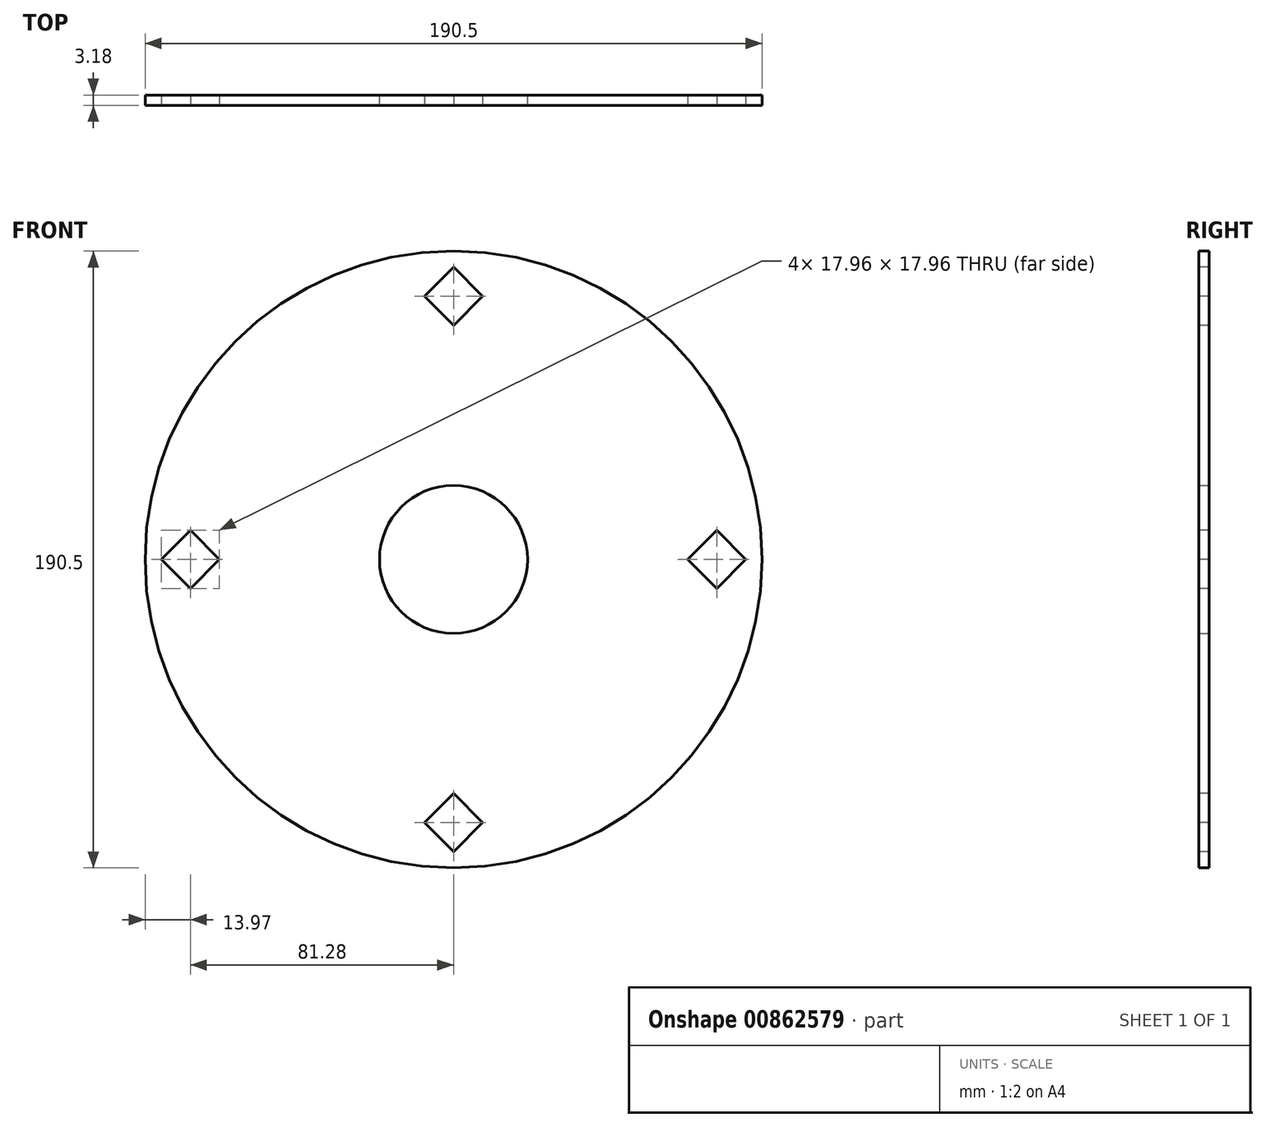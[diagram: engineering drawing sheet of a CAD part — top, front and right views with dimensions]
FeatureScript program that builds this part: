
annotation { "Feature Type Name" : "Feature", "Feature Type Description" : "" }
export const myFeature = defineFeature(function(context is Context, id is Id, definition is map)
    precondition{}
    {
        {
            var Q0;
            Q0=qCreatedBy(makeId("Front.planeOp"),FACE);
            var sketch = newSketch(context, id + "F0", { "sketchPlane" : qUnion([Q0])});
            skCircle(sketch, "E0", {"center": v(0, 0) * mm, "radius": 95.25 * mm});
            skSolve(sketch);
        }
        {
            var Q0;
            Q0=makeQuery(id+"F0.imprint","IMPRINT",FACE,{"disambiguationData":[TD([[makeQuery(id+"F0.imprint","IMPRINT",EDGE,{"derivedFrom":sQuery(id+"F0.wireOp",EDGE,"E0")}),1.0]])]});
            var sketch = newSketch(context, id + "F1", { "sketchPlane" : qUnion([Q0])});
            skCircle(sketch, "E1", {"center": v(0, 0) * mm, "radius": 22.86 * mm});
            skSolve(sketch);
        }
        {
            var Q0;
            Q0 = qSketchRegion(id + "F0", true);
            extrude(context, id + "F2", {"entities" : qUnion([Q0]), "depth" : 3.17 * mm, "offsetDistance" : 25.4 * mm});
        }
        {
            var Q0;
            Q0 = qSketchRegion(id + "F1", true);
            extrude(context, id + "F3", {"entities" : qUnion([Q0]), "operationType" : NewBodyOperationType.REMOVE, "depth" : 25.4 * mm, "offsetDistance" : 25.4 * mm});
        }
        {
            var Q0;
            Q0=makeQuery(id+"F2.opExtrude","CAP_FACE",FACE,{"disambiguationData":[OSD([sQuery(id+"F0.wireOp",EDGE,"E0")])],"isStart":false});
            var sketch = newSketch(context, id + "F4", { "sketchPlane" : qUnion([Q0])});
            skLineSegment(sketch, "E2", {"start": v(0, 0) * mm, "end": v(0, 95.25) * mm, "construction": true});
            skLineSegment(sketch, "E3.bottom", {"start": v(-72.3, 0) * mm, "end": v(-81.28, 8.98) * mm});
            skLineSegment(sketch, "E3.top", {"start": v(-81.28, -8.98) * mm, "end": v(-90.26, 0) * mm});
            skLineSegment(sketch, "E3.left", {"start": v(-72.3, 0) * mm, "end": v(-81.28, -8.98) * mm});
            skLineSegment(sketch, "E3.right", {"start": v(-81.28, 8.98) * mm, "end": v(-90.26, 0) * mm});
            skPoint(sketch, "E3.middle", {"position": v(-81.28, 0) * mm});
            skPoint(sketch, "E4.center", {"position": v(0, 0) * mm});
            skLineSegment(sketch, "E5", {"start": v(0, 0) * mm, "end": v(-81.28, 0) * mm, "construction": true});
            skPoint(sketch, "E6.center", {"position": v(-17.11, 0) * mm});
            skLineSegment(sketch, "E7.1.0", {"start": v(8.98, -81.28) * mm, "end": v(0, -90.26) * mm});
            skPoint(sketch, "E7.1.1", {"position": v(0, -81.28) * mm});
            skLineSegment(sketch, "E7.1.2", {"start": v(0, -72.3) * mm, "end": v(-8.98, -81.28) * mm});
            skLineSegment(sketch, "E7.1.3", {"start": v(-8.98, -81.28) * mm, "end": v(0, -90.26) * mm});
            skLineSegment(sketch, "E7.1.4", {"start": v(0, -72.3) * mm, "end": v(8.98, -81.28) * mm});
            skLineSegment(sketch, "E7.2.0", {"start": v(81.28, 8.98) * mm, "end": v(90.26, 0) * mm});
            skPoint(sketch, "E7.2.1", {"position": v(81.28, 0) * mm});
            skLineSegment(sketch, "E7.2.2", {"start": v(72.3, 0) * mm, "end": v(81.28, -8.98) * mm});
            skLineSegment(sketch, "E7.2.3", {"start": v(81.28, -8.98) * mm, "end": v(90.26, 0) * mm});
            skLineSegment(sketch, "E7.2.4", {"start": v(72.3, 0) * mm, "end": v(81.28, 8.98) * mm});
            skLineSegment(sketch, "E7.3.0", {"start": v(-8.98, 81.28) * mm, "end": v(0, 90.26) * mm});
            skPoint(sketch, "E7.3.1", {"position": v(0, 81.28) * mm});
            skLineSegment(sketch, "E7.3.2", {"start": v(0, 72.3) * mm, "end": v(8.98, 81.28) * mm});
            skLineSegment(sketch, "E7.3.3", {"start": v(8.98, 81.28) * mm, "end": v(0, 90.26) * mm});
            skLineSegment(sketch, "E7.3.4", {"start": v(0, 72.3) * mm, "end": v(-8.98, 81.28) * mm});
            skSolve(sketch);
        }
        {
            var Q0;
            Q0 = qSketchRegion(id + "F4", true);
            extrude(context, id + "F5", {"entities" : qUnion([Q0]), "operationType" : NewBodyOperationType.REMOVE, "oppositeDirection" : true, "depth" : 25.4 * mm, "offsetDistance" : 25.4 * mm});
        }
    });
